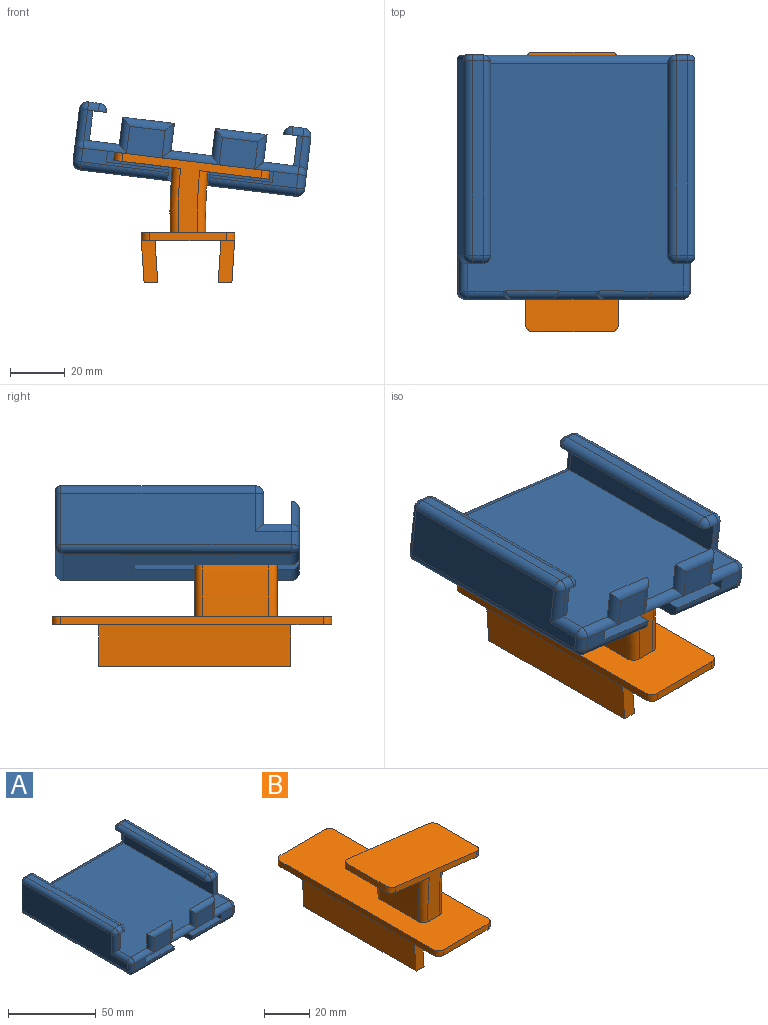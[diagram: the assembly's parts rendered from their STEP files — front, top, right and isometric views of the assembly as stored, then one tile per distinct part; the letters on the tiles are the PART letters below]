
ASSEMBLY  parts=2 mates=1
PART A: 78 faces, bbox 85x89x25 mm
  f0: plane 5x1mm, normal (0,1,0), area 4.8mm2, adj f9,f31,f70,f71
  f1: plane 5x1mm, normal (0,1,0), area 4.8mm2, adj f8,f39,f75,f76
  f2: plane 32x5mm, normal (0,-1,0), area 68mm2, adj f18,f19,f20,f53,f64,f66
  f3: plane 13x10mm, normal (0,-1,0), area 130mm2, adj f21,f49,f50,f51
  f4: plane 13x10mm, normal (0,-1,0), area 130mm2, adj f21,f45,f46,f47
  f5: plane 83x79mm, normal (0,0,1), area 6265mm2, adj f7,f10,f25,f26,f27,f28,f43,f44
  f6: plane 71x4mm, normal (0,0,1), area 284mm2, adj f29,f33,f34,f71
  f7: plane 73x11mm, normal (1,0,0), area 803mm2, adj f5,f8,f26,f56
  f8: plane 76x8mm, normal (0,0,-1), area 378.1mm2, adj f1,f7,f39,f40,f41,f42,f56
  f9: plane 76x8mm, normal (0,0,-1), area 378.1mm2, adj f0,f10,f31,f33,f34,f35,f54
  f10: plane 73x11mm, normal (-1,0,0), area 803mm2, adj f5,f9,f25,f54
  f11: plane 32x5mm, normal (0,-1,0), area 68mm2, adj f17,f22,f23,f44,f58,f59
  f12: plane 71x4mm, normal (0,0,1), area 284mm2, adj f37,f40,f41,f76
  f13: plane 84x19mm, normal (-1,0,0), area 1414mm2, adj f36,f37,f43,f58,f61,f74
  f14: plane 83x79mm, normal (0,0,-1), area 5702mm2, adj f17,f18,f24,f59,f61,f62,f63,f64
  f15: plane 84x19mm, normal (1,0,0), area 1414mm2, adj f29,f30,f52,f63,f66,f69
  f16: plane 81x5mm, normal (0,1,0), area 405mm2, adj f55,f62,f69,f74
  f17: plane 60x4mm, normal (1,0,0), area 238.1mm2, adj f11,f14,f23,f24,f59
  f18: plane 60x4mm, normal (-1,0,0), area 238.1mm2, adj f2,f14,f19,f24,f64
  f19: plane 60x23mm, normal (0,0,1), area 1380mm2, adj f2,f18,f20,f24
  f20: plane 60x4mm, normal (-1,0,0), area 240mm2, adj f2,f19,f21,f24
  f21: plane 61x60mm, normal (0,0,-1), area 3660mm2, adj f3,f4,f20,f22,f24,f44,f48,f53
  f22: plane 60x4mm, normal (1,0,0), area 240mm2, adj f11,f21,f23,f24
  f23: plane 60x23mm, normal (0,0,1), area 1380mm2, adj f11,f17,f22,f24
  f24: plane 61x8mm, normal (0,-1,0), area 304mm2, adj f14,f17,f18,f19,f20,f21,f22,f23
  f25: plane 11x2mm, normal (0,-1,0), area 22mm2, adj f5,f10,f30,f34
  f26: plane 11x2mm, normal (0,-1,0), area 22mm2, adj f5,f7,f36,f40
  f27: plane 19x10mm, normal (0,1,0), area 190mm2, adj f5,f45,f46,f47
  f28: plane 19x10mm, normal (0,1,0), area 190mm2, adj f5,f49,f50,f51
  f29: cylinder r=3mm len=71mm, axis (0,-1,0), area 334.6mm2, adj f6,f15,f32,f70
  f30: cylinder r=3mm len=14mm, axis (0,0,-1), area 57mm2, adj f15,f25,f32,f52
  f31: cylinder r=3mm len=3mm, axis (0,0,1), area 3mm2, adj f0,f9,f72
  f32: sphere r=3mm, area 14.1mm2, adj f29,f30,f34
  f33: cylinder r=3mm len=71mm, axis (0,1,0), area 332.9mm2, adj f6,f9,f35,f72
  f34: cylinder r=3mm len=4mm, axis (1,0,0), area 18.8mm2, adj f6,f9,f25,f32,f35
  f35: sphere r=3mm, area 14.1mm2, adj f9,f33,f34
  f36: cylinder r=3mm len=14mm, axis (0,0,1), area 57mm2, adj f13,f26,f38,f43
  f37: cylinder r=3mm len=71mm, axis (0,-1,0), area 334.6mm2, adj f12,f13,f38,f75
  f38: sphere r=3mm, area 14.1mm2, adj f36,f37,f40
  f39: cylinder r=3mm len=3mm, axis (0,0,-1), area 3mm2, adj f1,f8,f77
  f40: cylinder r=3mm len=4mm, axis (-1,0,0), area 18.8mm2, adj f8,f12,f26,f38,f42
  f41: cylinder r=3mm len=71mm, axis (0,1,0), area 332.9mm2, adj f8,f12,f42,f77
  f42: sphere r=3mm, area 14.1mm2, adj f8,f40,f41
  f43: cylinder r=3mm len=13mm, axis (0,1,0), area 52.3mm2, adj f5,f13,f36,f57
  f44: cylinder r=3mm len=16mm, axis (-1,0,0), area 66.4mm2, adj f5,f11,f21,f45,f57
  f45: cylinder r=3mm len=13mm, axis (0,0,-1), area 47.1mm2, adj f4,f27,f44,f46
  f46: cylinder r=3mm len=19mm, axis (1,0,0), area 79.3mm2, adj f4,f27,f45,f47
  f47: cylinder r=3mm len=13mm, axis (0,0,-1), area 47.1mm2, adj f4,f27,f46,f48
  f48: cylinder r=3mm len=21mm, axis (-1,0,0), area 81mm2, adj f5,f21,f47,f49
  f49: cylinder r=3mm len=13mm, axis (0,0,1), area 47.1mm2, adj f3,f28,f48,f50
  f50: cylinder r=3mm len=19mm, axis (1,0,0), area 79.3mm2, adj f3,f28,f49,f51
  f51: cylinder r=3mm len=13mm, axis (0,0,1), area 47.1mm2, adj f3,f28,f50,f53
  f52: cylinder r=3mm len=13mm, axis (0,-1,0), area 52.3mm2, adj f5,f15,f30,f67
  f53: cylinder r=3mm len=16mm, axis (-1,0,0), area 66.4mm2, adj f2,f5,f21,f51,f67
  f54: cylinder r=3mm len=14mm, axis (0,0,1), area 57mm2, adj f9,f10,f55,f69
  f55: cylinder r=3mm len=81mm, axis (1,0,0), area 363.7mm2, adj f5,f16,f54,f56
  f56: cylinder r=3mm len=14mm, axis (0,0,-1), area 57mm2, adj f7,f8,f55,f74
  f57: sphere r=3mm, area 14.1mm2, adj f43,f44,f58
  f58: cylinder r=3mm len=5mm, axis (0,0,-1), area 23.6mm2, adj f11,f13,f57,f60
  f59: cylinder r=3mm len=32mm, axis (1,0,0), area 150.8mm2, adj f11,f14,f17,f60
  f60: sphere r=3mm, area 14.1mm2, adj f58,f59,f61
  f61: cylinder r=3mm len=84mm, axis (0,-1,0), area 394.1mm2, adj f13,f14,f60,f73
  f62: cylinder r=3mm len=81mm, axis (-1,0,0), area 378.3mm2, adj f14,f16,f68,f73
  f63: cylinder r=3mm len=84mm, axis (0,1,0), area 394.1mm2, adj f14,f15,f65,f68
  f64: cylinder r=3mm len=32mm, axis (1,0,0), area 150.8mm2, adj f2,f14,f18,f65
  f65: sphere r=3mm, area 14.1mm2, adj f63,f64,f66
  f66: cylinder r=3mm len=5mm, axis (0,0,1), area 23.6mm2, adj f2,f15,f65,f67
  f67: sphere r=3mm, area 14.1mm2, adj f52,f53,f66
  f68: bspline ~3.65x3mm, area 9.7mm2, adj f62,f63,f69
  f69: cylinder r=2mm len=19mm, axis (0,0,-1), area 59.7mm2, adj f15,f16,f54,f68,f70
  f70: torus R=1mm, axis (0,-1,0), area 11.2mm2, adj f0,f29,f69,f71
  f71: cylinder r=2mm len=4mm, axis (1,0,0), area 12.6mm2, adj f0,f6,f70,f72
  f72: bspline ~3.65x3mm, area 9.7mm2, adj f31,f33,f71
  f73: bspline ~3.65x3mm, area 9.7mm2, adj f61,f62,f74
  f74: cylinder r=2mm len=19mm, axis (0,0,1), area 59.7mm2, adj f13,f16,f56,f73,f75
  f75: torus R=1mm, axis (0,-1,0), area 11.2mm2, adj f1,f37,f74,f76
  f76: cylinder r=2mm len=4mm, axis (1,0,0), area 12.6mm2, adj f1,f12,f75,f77
  f77: bspline ~3.65x3mm, area 9.7mm2, adj f39,f41,f76
PART B: 37 faces, bbox 57x102x47.4 mm
  f0: plane 102x34mm, normal (0,0,-1), area 2760.3mm2, adj f1,f2,f3,f4,f20,f21,f23,f25
  f1: plane 96x3mm, normal (-1,0,0), area 288mm2, adj f0,f5,f26,f33,f36
  f2: plane 28x3mm, normal (0,-1,0), area 84mm2, adj f0,f5,f33,f34
  f3: plane 96x3mm, normal (1,0,0), area 288mm2, adj f0,f5,f22,f34,f35
  f4: plane 28x3mm, normal (0,1,0), area 84mm2, adj f0,f5,f35,f36
  f5: plane 102.04x34.04mm, normal (0,0,1), area 3078mm2, adj f1,f2,f3,f4,f6,f7,f8,f9
  f6: plane 50.99x29mm, normal (0,1,0), area 314.1mm2, adj f5,f10,f11,f14,f15,f18,f31,f32
  f7: cylinder r=196.5mm len=24mm, axis (0,1,0), area 571.5mm2, adj f5,f10,f30,f31
  f8: plane 50.99x29mm, normal (0,-1,0), area 314.1mm2, adj f5,f10,f11,f14,f16,f17,f29,f30
  f9: cylinder r=183.5mm len=24mm, axis (0,1,0), area 533.7mm2, adj f5,f11,f29,f32
  f10: plane 30.04x24.36mm, normal (-0.12,0,-0.99), area 645mm2, adj f6,f7,f8,f12,f15,f16,f30,f31
  f11: plane 30.04x25.35mm, normal (-0.12,0,-0.99), area 675mm2, adj f6,f8,f9,f13,f17,f18,f29,f32
  f12: plane 24x2.98mm, normal (-0.99,0,0.12), area 72mm2, adj f10,f14,f15,f16
  f13: plane 24x2.98mm, normal (0.99,0,-0.12), area 72mm2, adj f11,f14,f17,f18
  f14: plane 56.58x30mm, normal (0.12,0,0.99), area 1702.3mm2, adj f6,f8,f12,f13,f15,f16,f17,f18
  f15: cylinder r=3mm len=3.34mm, axis (0.12,0,0.99), area 14.1mm2, adj f6,f10,f12,f14
  f16: cylinder r=3mm len=3.34mm, axis (0.12,0,0.99), area 14.1mm2, adj f8,f10,f12,f14
  f17: cylinder r=3mm len=3.34mm, axis (-0.12,0,-0.99), area 14.1mm2, adj f8,f11,f13,f14
  f18: cylinder r=3mm len=3.34mm, axis (-0.12,0,-0.99), area 14.1mm2, adj f6,f11,f13,f14
  f19: plane 70x5mm, normal (0,0,-1), area 350mm2, adj f20,f21,f22,f23
  f20: plane 70x15mm, normal (-1,0,0.07), area 1052.3mm2, adj f0,f19,f21,f23
  f21: plane 15x6mm, normal (0,1,0), area 75mm2, adj f0,f19,f20,f22
  f22: plane 70x15mm, normal (1,0,-0.07), area 1052.3mm2, adj f3,f19,f21,f23
  f23: plane 15x6mm, normal (0,-1,0), area 75mm2, adj f0,f19,f20,f22
  f24: plane 70x5mm, normal (0,0,-1), area 350mm2, adj f25,f26,f27,f28
  f25: plane 15x6mm, normal (0,-1,0), area 75mm2, adj f0,f24,f26,f28
  f26: plane 70x15mm, normal (-1,0,-0.07), area 1052.3mm2, adj f1,f24,f25,f27
  f27: plane 15x6mm, normal (0,1,0), area 75mm2, adj f0,f24,f26,f28
  f28: plane 70x15mm, normal (1,0,0.07), area 1052.3mm2, adj f0,f24,f25,f27
  f29: torus R=186.5mm, axis (0,-1,0), area 105.4mm2, adj f5,f8,f9,f11
  f30: torus R=193.5mm, axis (0,-1,0), area 111.6mm2, adj f5,f7,f8,f10
  f31: torus R=193.5mm, axis (0,1,0), area 111.6mm2, adj f5,f6,f7,f10
  f32: torus R=186.5mm, axis (0,1,0), area 105.4mm2, adj f5,f6,f9,f11
  f33: cylinder r=3mm len=3mm, axis (0,0,1), area 14.1mm2, adj f0,f1,f2,f5
  f34: cylinder r=3mm len=3mm, axis (0,0,-1), area 14.1mm2, adj f0,f2,f3,f5
  f35: cylinder r=3mm len=3mm, axis (0,0,1), area 14.1mm2, adj f0,f3,f4,f5
  f36: cylinder r=3mm len=3mm, axis (0,0,-1), area 14.1mm2, adj f0,f1,f4,f5
PLACE A rot(axis=(0,1,0),6.9deg) t=(-82.43,-30.9,117.87)mm
PLACE B t=(-82.38,7.24,96.81)mm
MATE planar A.f21 <-> B.f14  axis (-0.12,0,-0.99) through (-81.46,-0.9,125.81)mm
